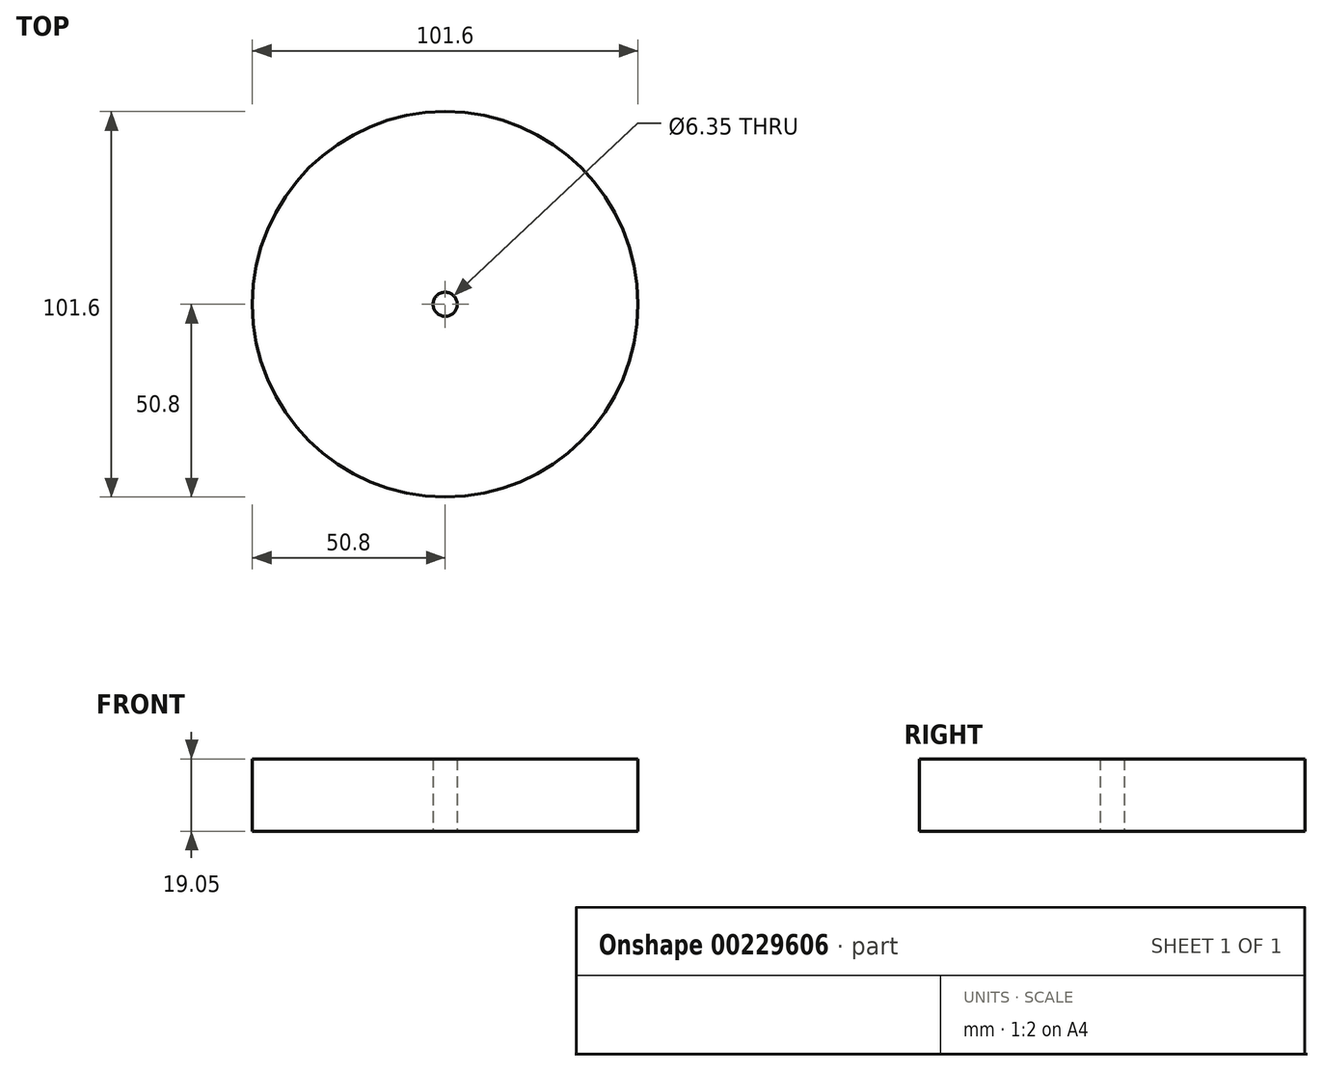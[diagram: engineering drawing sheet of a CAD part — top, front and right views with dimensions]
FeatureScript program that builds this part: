
annotation { "Feature Type Name" : "Feature", "Feature Type Description" : "" }
export const myFeature = defineFeature(function(context is Context, id is Id, definition is map)
    precondition{}
    {
        {
            var Q0;
            Q0=qCreatedBy(makeId("Top.planeOp"),FACE);
            var sketch = newSketch(context, id + "F0", { "sketchPlane" : qUnion([Q0])});
            skCircle(sketch, "E0", {"center": v(0, 0) * mm, "radius": 50.8 * mm});
            skCircle(sketch, "E1", {"center": v(0, 0) * mm, "radius": 3.18 * mm});
            skSolve(sketch);
        }
        {
            var Q0;
            Q0=makeQuery(id+"F0.imprint","IMPRINT",FACE,{"disambiguationData":[TD([[makeQuery(id+"F0.imprint","IMPRINT",EDGE,{"derivedFrom":sQuery(id+"F0.wireOp",EDGE,"E0")}),1.0]])]});
            extrude(context, id + "F1", {"entities" : qUnion([Q0]), "depth" : 19.05 * mm});
        }
    });
